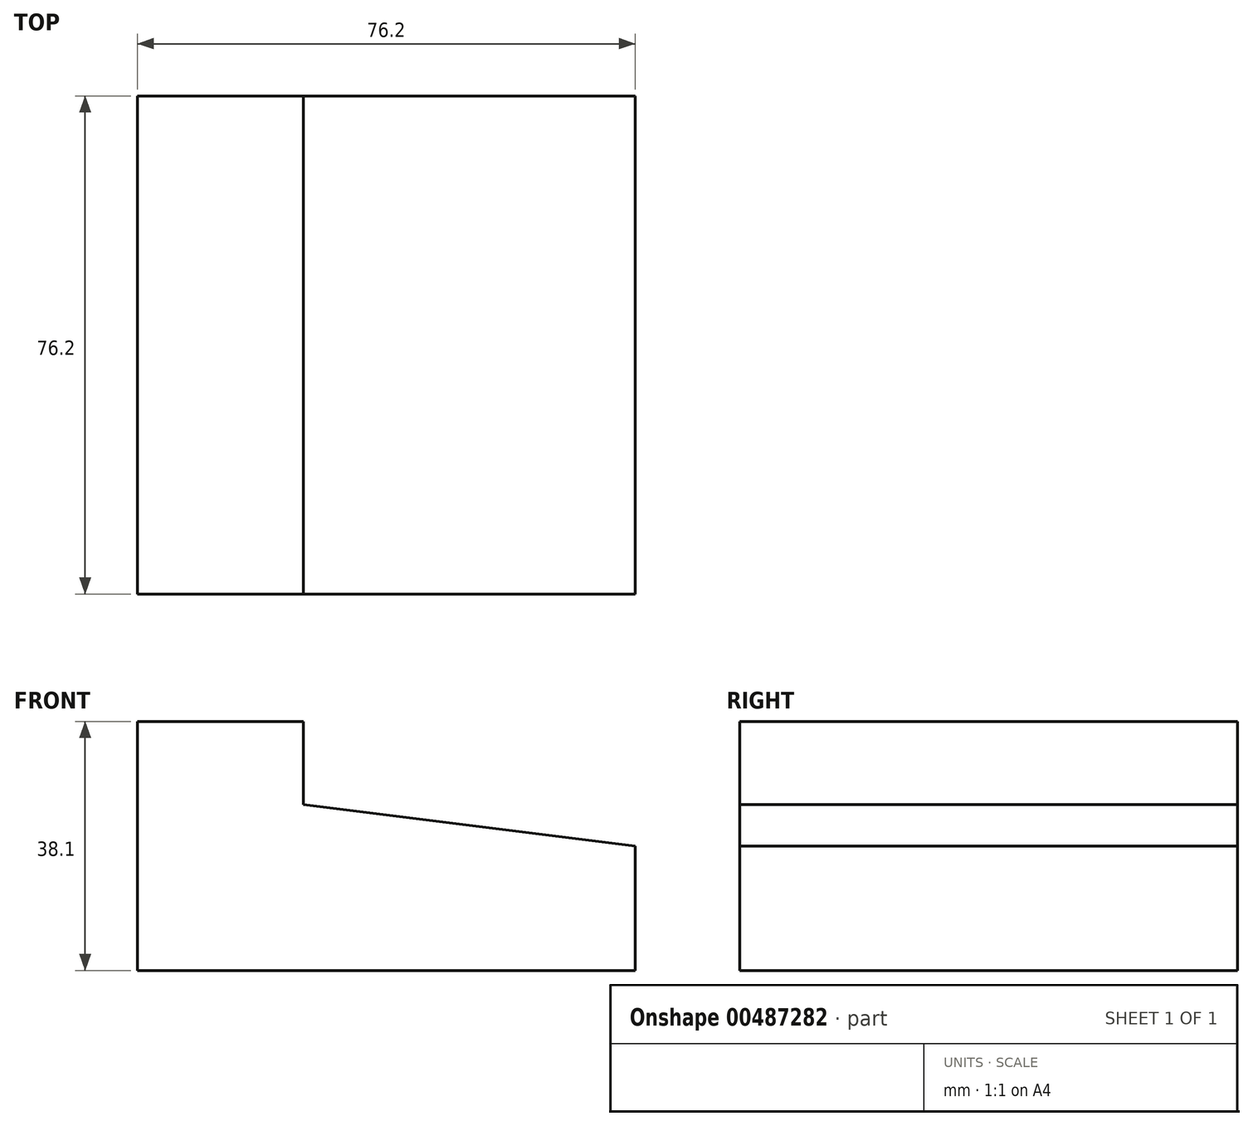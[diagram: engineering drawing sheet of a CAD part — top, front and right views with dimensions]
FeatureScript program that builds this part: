
annotation { "Feature Type Name" : "Feature", "Feature Type Description" : "" }
export const myFeature = defineFeature(function(context is Context, id is Id, definition is map)
    precondition{}
    {
        {
            var Q0;
            Q0=qCreatedBy(makeId("Top.planeOp"),FACE);
            var sketch = newSketch(context, id + "F0", { "sketchPlane" : qUnion([Q0])});
            skLineSegment(sketch, "E0", {"start": v(-40.86, -37.37) * mm, "end": v(35.34, -37.37) * mm});
            skLineSegment(sketch, "E1", {"start": v(35.34, -37.37) * mm, "end": v(35.34, 38.83) * mm});
            skLineSegment(sketch, "E2", {"start": v(35.34, 38.83) * mm, "end": v(-40.86, 38.83) * mm});
            skLineSegment(sketch, "E3", {"start": v(-40.86, 38.83) * mm, "end": v(-40.86, -37.37) * mm});
            skSolve(sketch);
        }
        {
            var Q0;
            Q0=makeQuery(id+"F0.imprint","IMPRINT",FACE,{"disambiguationData":[TD([[makeQuery(id+"F0.imprint","IMPRINT",EDGE,{"derivedFrom":sQuery(id+"F0.wireOp",EDGE,"E0")}),1.0]])]});
            var sketch = newSketch(context, id + "F1", { "sketchPlane" : qUnion([Q0])});
            skSolve(sketch);
        }
        {
            var Q0;
            Q0 = qSketchRegion(id + "F1", true);
            var Q1;
            Q1=makeQuery(id+"F0.imprint","IMPRINT",FACE,{"disambiguationData":[TD([[makeQuery(id+"F0.imprint","IMPRINT",EDGE,{"derivedFrom":sQuery(id+"F0.wireOp",EDGE,"E0")}),1.0]])]});
            extrude(context, id + "F2", {"entities" : qUnion([Q0, Q1]), "depth" : 38.1 * mm});
        }
        {
            var Q0;
            Q0=makeQuery(id+"F2.opExtrude","SWEPT_FACE",FACE,{"disambiguationData":[OSD([sQuery(id+"F0.wireOp",EDGE,"E0")])]});
            var sketch = newSketch(context, id + "F3", { "sketchPlane" : qUnion([Q0])});
            skLineSegment(sketch, "E4", {"start": v(-40.86, 38.1) * mm, "end": v(-15.46, 38.1) * mm});
            skLineSegment(sketch, "E5", {"start": v(-15.46, 38.1) * mm, "end": v(-15.46, 25.4) * mm});
            skLineSegment(sketch, "E6", {"start": v(-15.46, 25.4) * mm, "end": v(35.34, 19.05) * mm});
            skLineSegment(sketch, "E7", {"start": v(35.34, 19.05) * mm, "end": v(35.34, 0) * mm});
            skSolve(sketch);
        }
        {
            var Q0;
            {var subQ0=sQuery(id+"F3.wireOp",EDGE,"E5");Q0=makeQuery(id+"F3.imprint","IMPRINT",FACE,{"disambiguationData":[TD([[makeQuery(id+"F3.imprint","IMPRINT",EDGE,{"derivedFrom":subQ0}),1.0]])]});}
            extrude(context, id + "F4", {"entities" : qUnion([Q0]), "operationType" : NewBodyOperationType.REMOVE, "endBound" : BoundingType.THROUGH_ALL, "oppositeDirection" : true, "depth" : 25.4 * mm});
        }
    });
